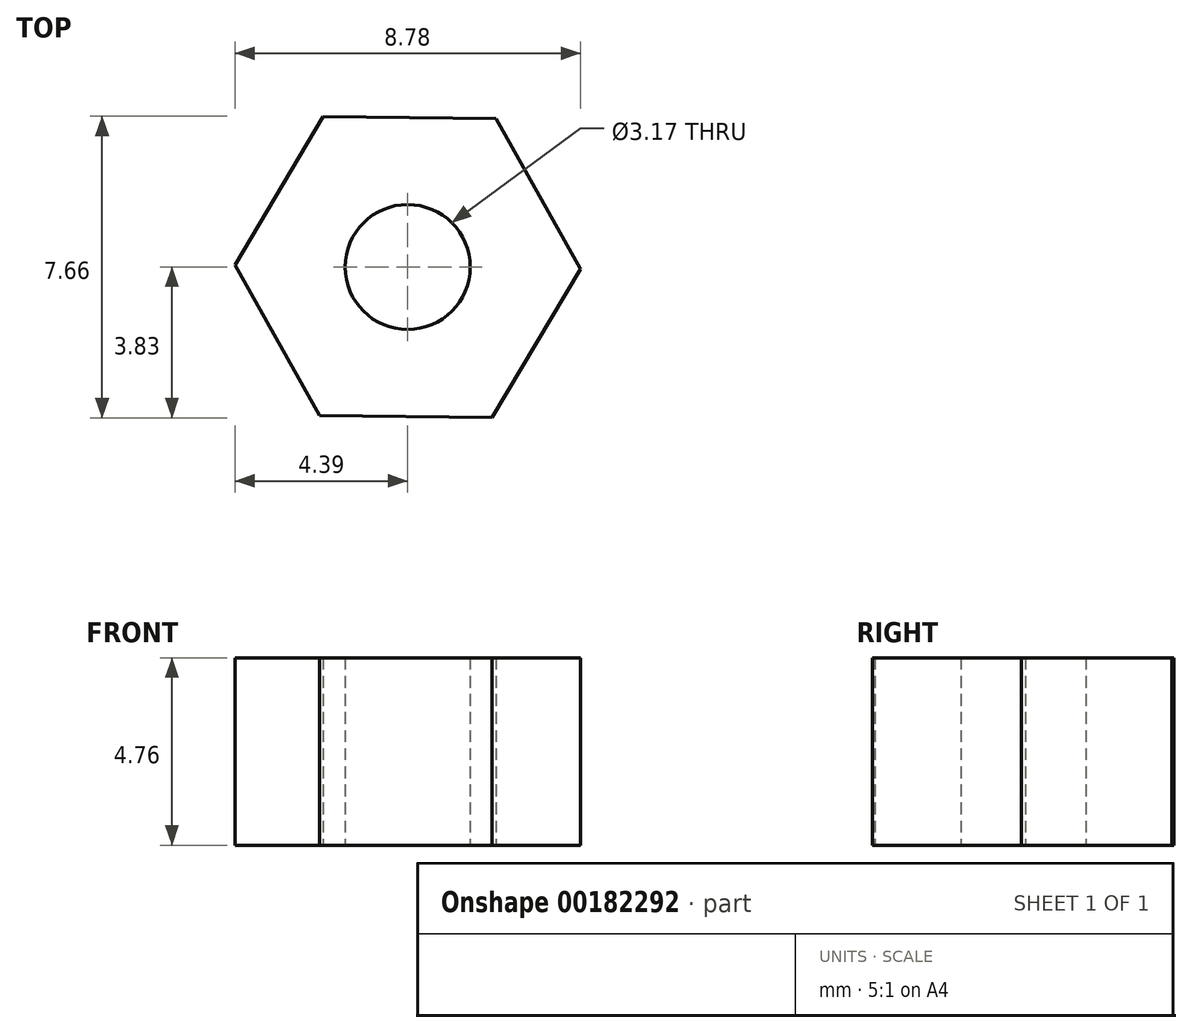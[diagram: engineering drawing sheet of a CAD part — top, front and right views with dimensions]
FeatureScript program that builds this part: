
annotation { "Feature Type Name" : "Feature", "Feature Type Description" : "" }
export const myFeature = defineFeature(function(context is Context, id is Id, definition is map)
    precondition{}
    {
        {
            var Q0;
            Q0=qCreatedBy(makeId("Top.planeOp"),FACE);
            var sketch = newSketch(context, id + "F0", { "sketchPlane" : qUnion([Q0])});
            skCircle(sketch, "E0.cCircle", {"center": v(0, 0) * mm, "radius": 3.8 * mm, "construction": true});
            skLineSegment(sketch, "E0.0", {"start": v(2.24, 3.77) * mm, "end": v(4.39, -0.05) * mm});
            skLineSegment(sketch, "E0.1", {"start": v(4.39, -0.05) * mm, "end": v(2.15, -3.83) * mm});
            skLineSegment(sketch, "E0.2", {"start": v(2.15, -3.83) * mm, "end": v(-2.24, -3.77) * mm});
            skLineSegment(sketch, "E0.3", {"start": v(-2.24, -3.77) * mm, "end": v(-4.39, 0.05) * mm});
            skLineSegment(sketch, "E0.4", {"start": v(-4.39, 0.05) * mm, "end": v(-2.15, 3.83) * mm});
            skLineSegment(sketch, "E0.5", {"start": v(-2.15, 3.83) * mm, "end": v(2.24, 3.77) * mm});
            skPoint(sketch, "E0.0.midPoint", {"position": v(3.31, 1.86) * mm});
            skCircle(sketch, "E1", {"center": v(0, 0) * mm, "radius": 1.59 * mm});
            skSolve(sketch);
        }
        {
            var Q0;
            Q0=makeQuery(id+"F0.imprint","IMPRINT",FACE,{"disambiguationData":[TD([[makeQuery(id+"F0.imprint","IMPRINT",EDGE,{"derivedFrom":sQuery(id+"F0.wireOp",EDGE,"E0.0")}),-1.0]])]});
            extrude(context, id + "F1", {"entities" : qUnion([Q0]), "depth" : 4.76 * mm});
        }
    });
